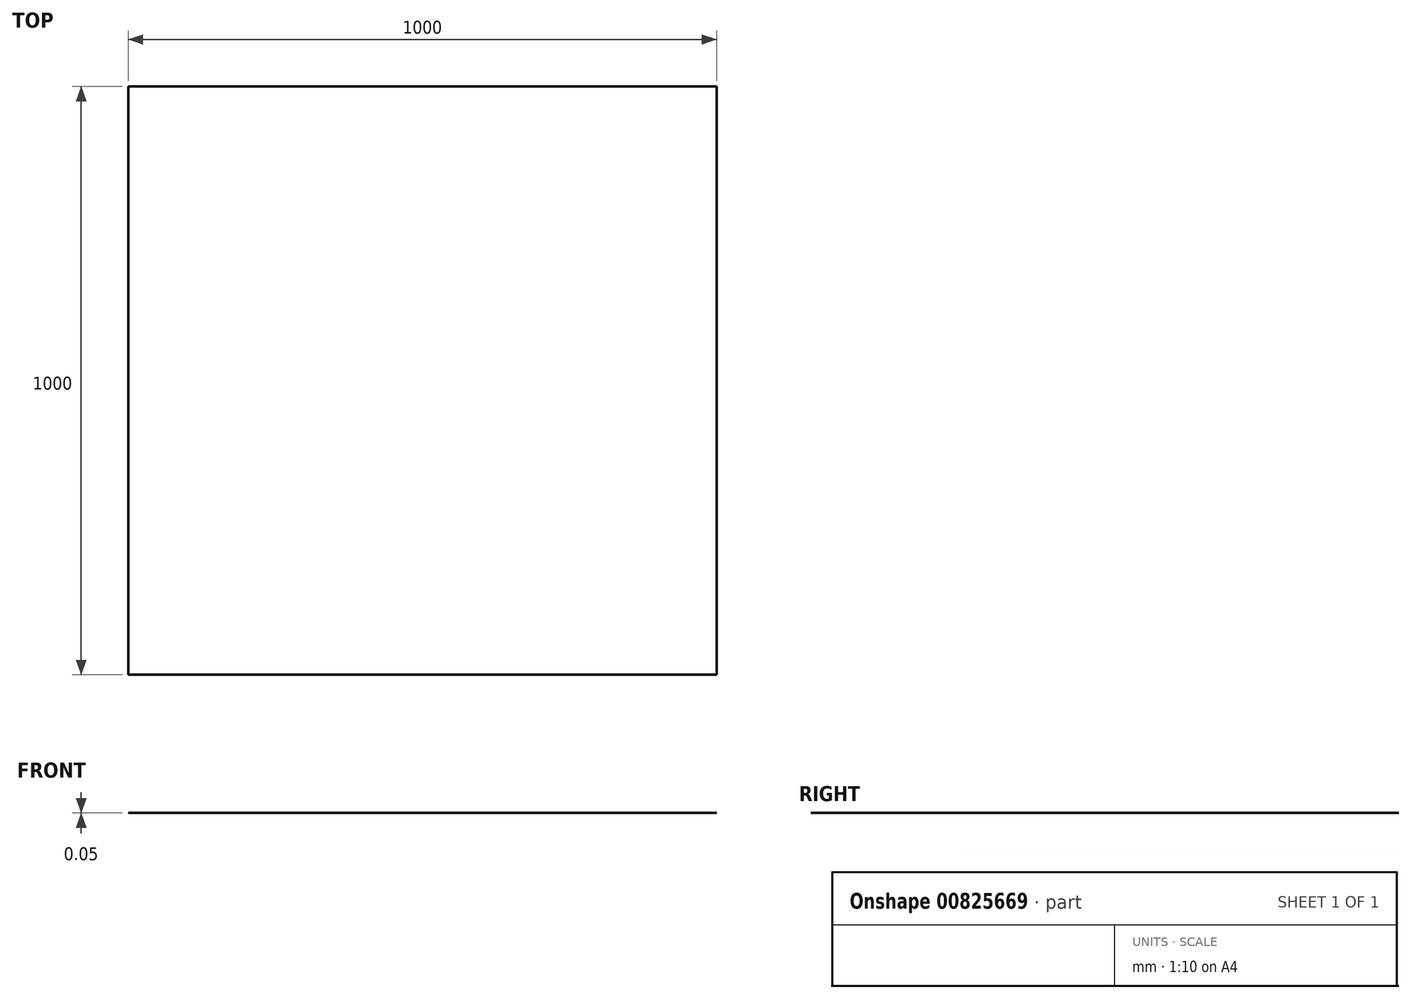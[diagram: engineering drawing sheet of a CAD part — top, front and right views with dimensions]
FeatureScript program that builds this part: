
annotation { "Feature Type Name" : "Feature", "Feature Type Description" : "" }
export const myFeature = defineFeature(function(context is Context, id is Id, definition is map)
    precondition{}
    {
        {
            var Q0;
            Q0=qCreatedBy(makeId("Top.planeOp"),FACE);
            var sketch = newSketch(context, id + "F0", { "sketchPlane" : qUnion([Q0])});
            skLineSegment(sketch, "E0.bottom", {"start": v(-496.92, 532.77) * mm, "end": v(503.08, 532.77) * mm});
            skLineSegment(sketch, "E0.top", {"start": v(-496.92, -467.23) * mm, "end": v(503.08, -467.23) * mm});
            skLineSegment(sketch, "E0.left", {"start": v(-496.92, 532.77) * mm, "end": v(-496.92, -467.23) * mm});
            skLineSegment(sketch, "E0.right", {"start": v(503.08, 532.77) * mm, "end": v(503.08, -467.23) * mm});
            skSolve(sketch);
        }
        {
            var Q0;
            Q0=makeQuery(id+"F0.imprint","IMPRINT",FACE,{"disambiguationData":[TD([[makeQuery(id+"F0.imprint","IMPRINT",EDGE,{"derivedFrom":sQuery(id+"F0.wireOp",EDGE,"E0.bottom")}),-1.0]])]});
            extrude(context, id + "F1", {"entities" : qUnion([Q0]), "depth" : 0.05 * mm, "offsetDistance" : 25 * mm});
        }
    });
